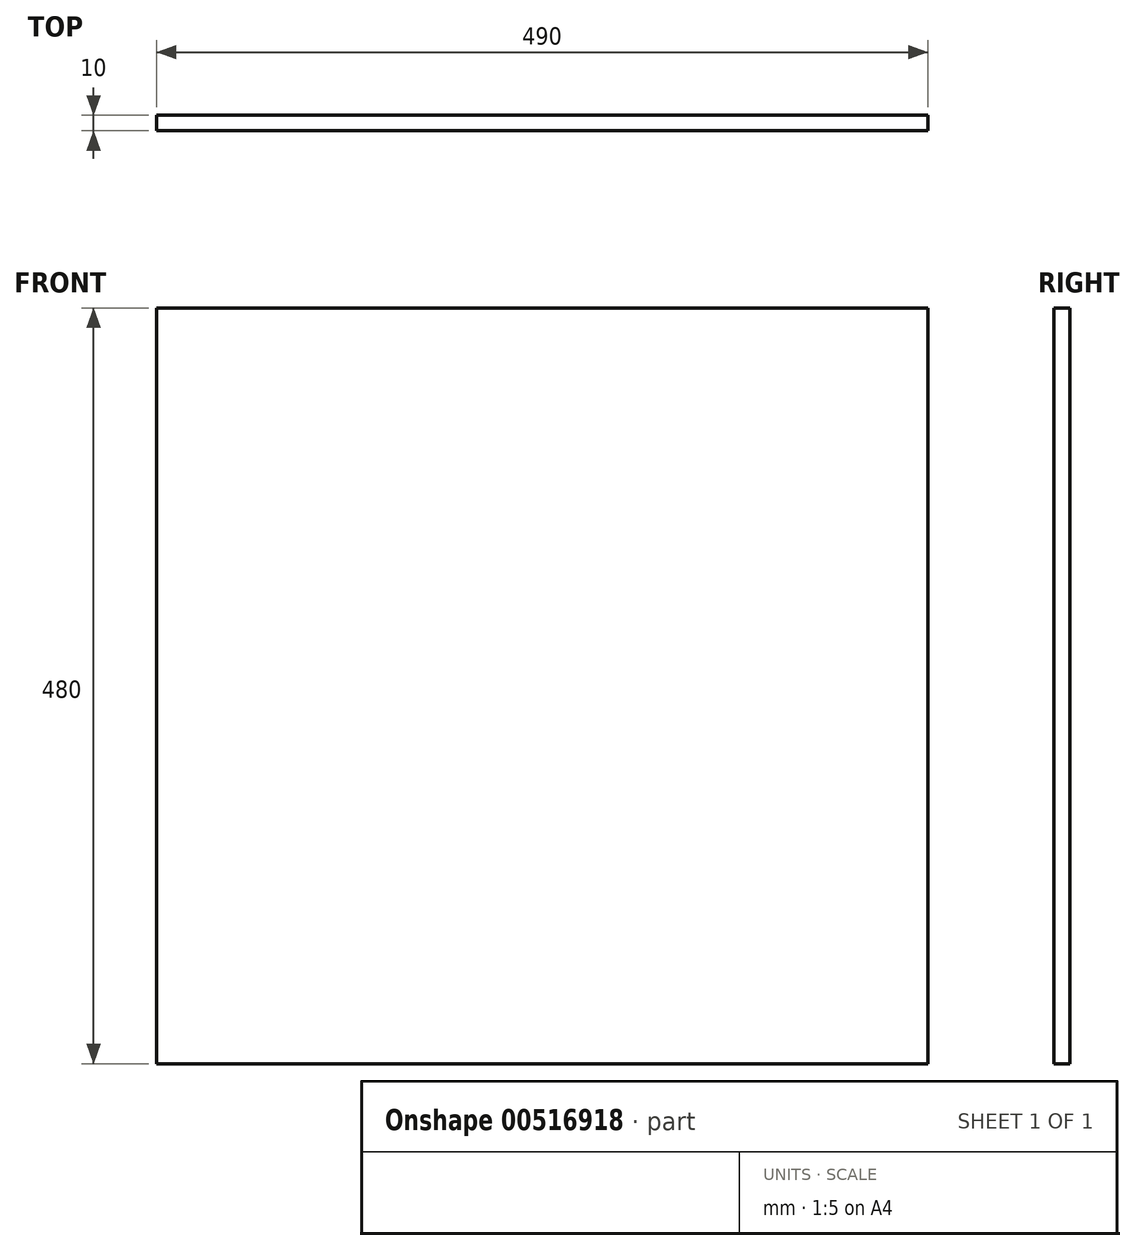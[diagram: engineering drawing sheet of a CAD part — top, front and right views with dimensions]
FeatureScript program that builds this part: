
annotation { "Feature Type Name" : "Feature", "Feature Type Description" : "" }
export const myFeature = defineFeature(function(context is Context, id is Id, definition is map)
    precondition{}
    {
        {
            var Q0;
            Q0=qCreatedBy(makeId("Front.planeOp"),FACE);
            var sketch = newSketch(context, id + "F0", { "sketchPlane" : qUnion([Q0])});
            skLineSegment(sketch, "E0.bottom", {"start": v(-245, 240) * mm, "end": v(245, 240) * mm});
            skLineSegment(sketch, "E0.top", {"start": v(-245, -240) * mm, "end": v(245, -240) * mm});
            skLineSegment(sketch, "E0.left", {"start": v(-245, 240) * mm, "end": v(-245, -240) * mm});
            skLineSegment(sketch, "E0.right", {"start": v(245, 240) * mm, "end": v(245, -240) * mm});
            skPoint(sketch, "E0.middle", {"position": v(0, 0) * mm});
            skSolve(sketch);
        }
        {
            var Q0;
            Q0=makeQuery(id+"F0.imprint","IMPRINT",FACE,{"disambiguationData":[TD([[makeQuery(id+"F0.imprint","IMPRINT",EDGE,{"derivedFrom":sQuery(id+"F0.wireOp",EDGE,"E0.bottom")}),-1.0]])]});
            extrude(context, id + "F1", {"entities" : qUnion([Q0]), "depth" : 10 * mm, "offsetDistance" : 25 * mm});
        }
    });
